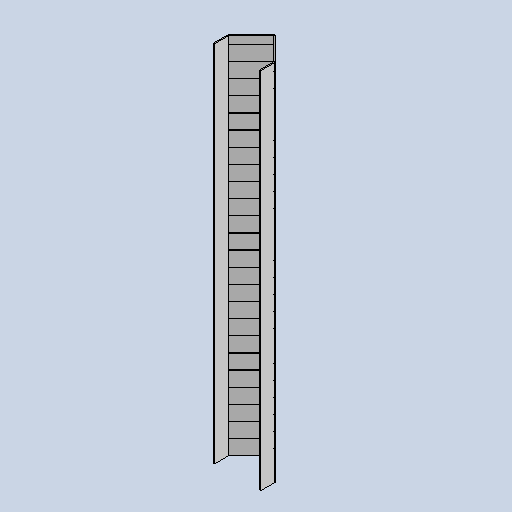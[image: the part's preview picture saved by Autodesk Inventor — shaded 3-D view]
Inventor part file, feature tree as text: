
AUTODESK INVENTOR PART (.ipt)
format: ipt  version: 2025.3 (Build 293356030, 356C)  size: 782,848 bytes
history: native  units: mm
features: sheet_metal_op x3, sketch x3, other x3, mirror x1
ambient origin geometry x8: Origin, YZ Plane, XZ Plane, XY Plane, X Axis, Y Axis, Z Axis, Center Point
bodies: Body1 (feature_tree)
feature tree (10):
  sheet_metal_op  "Contour Flange1"
  mirror  "Mirror2"
  sketch  "Sketch3"  dims[d15=10.0mm]
  other  "Plate1"
  sheet_metal_op  "Bend1"
  sheet_metal_op  "Corner1"
  sketch  "Sketch5"  dims[d19=1.0mm d20=1.0mm d21=0.8mm d22=0.8mm d23=0.4mm d24=1.6mm d25=0.8mm d26=245.0mm d27=0.8mm d28=0.8mm d29=3.2mm d30=0.8mm d31=0.8mm d32=32.0mm d33=90.0deg d111=0.2mm d112=28.0mm d113=5.0mm d114=0.5mm d115=240.0mm d116=10.0mm d73=10.0mm d75=10.0mm d97=5.0mm d98=0.8mm d99=0.0mm d101=0.5mm d102=0.872665mm d103=0.5mm d104=0.872665mm]
  sketch  "Sketch Rectangular Pattern3"  dims[d18=1.0mm]
  other  "Cut3"
  other  "Definition1"
